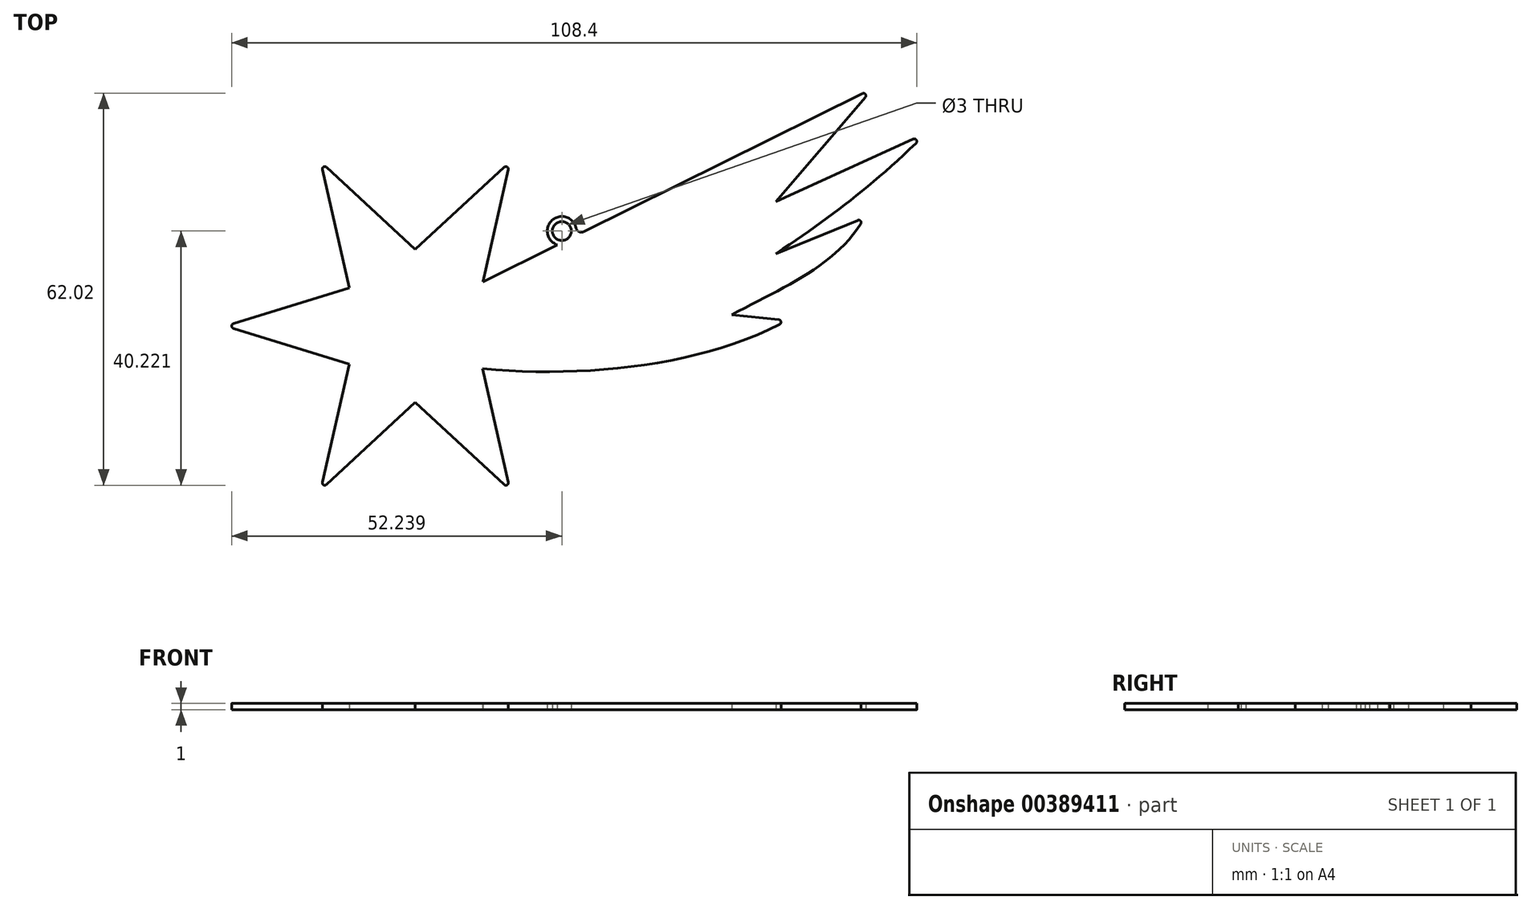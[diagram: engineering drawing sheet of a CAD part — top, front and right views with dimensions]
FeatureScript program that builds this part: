
annotation { "Feature Type Name" : "Feature", "Feature Type Description" : "" }
export const myFeature = defineFeature(function(context is Context, id is Id, definition is map)
    precondition{}
    {
        {
            var Q0;
            Q0=qCreatedBy(makeId("Top.planeOp"),FACE);
            var sketch = newSketch(context, id + "F0", { "sketchPlane" : qUnion([Q0])});
            skCircle(sketch, "E0.cCircle", {"center": v(0, 0) * mm, "radius": 30 * mm, "construction": true});
            skLineSegment(sketch, "E0.0", {"start": v(-30, 0) * mm, "end": v(-15, 25.98) * mm, "construction": true});
            skLineSegment(sketch, "E0.1", {"start": v(-15, 25.98) * mm, "end": v(15, 25.98) * mm, "construction": true});
            skLineSegment(sketch, "E0.2", {"start": v(15, 25.98) * mm, "end": v(30, 0) * mm, "construction": true});
            skLineSegment(sketch, "E0.3", {"start": v(30, 0) * mm, "end": v(15, -25.98) * mm, "construction": true});
            skLineSegment(sketch, "E0.4", {"start": v(15, -25.98) * mm, "end": v(-15, -25.98) * mm, "construction": true});
            skLineSegment(sketch, "E0.5", {"start": v(-15, -25.98) * mm, "end": v(-30, 0) * mm, "construction": true});
            skCircle(sketch, "E1.cCircle", {"center": v(0, 0) * mm, "radius": 12.09 * mm, "construction": true});
            skLineSegment(sketch, "E1.0", {"start": v(0, 12.09) * mm, "end": v(10.47, 6.04) * mm, "construction": true});
            skLineSegment(sketch, "E1.1", {"start": v(10.47, 6.04) * mm, "end": v(10.47, -6.04) * mm, "construction": true});
            skLineSegment(sketch, "E1.2", {"start": v(10.47, -6.04) * mm, "end": v(0, -12.09) * mm, "construction": true});
            skLineSegment(sketch, "E1.3", {"start": v(0, -12.09) * mm, "end": v(-10.47, -6.04) * mm, "construction": true});
            skLineSegment(sketch, "E1.4", {"start": v(-10.47, -6.04) * mm, "end": v(-10.47, 6.04) * mm, "construction": true});
            skLineSegment(sketch, "E1.5", {"start": v(-10.47, 6.04) * mm, "end": v(0, 12.09) * mm, "construction": true});
            skLineSegment(sketch, "E2", {"start": v(-15, 25.98) * mm, "end": v(-10.47, 6.04) * mm});
            skLineSegment(sketch, "E3", {"start": v(-30, 0) * mm, "end": v(-10.47, 6.04) * mm});
            skLineSegment(sketch, "E4", {"start": v(-30, 0) * mm, "end": v(-10.47, -6.04) * mm});
            skLineSegment(sketch, "E5", {"start": v(-10.47, -6.04) * mm, "end": v(-15, -25.98) * mm});
            skLineSegment(sketch, "E6", {"start": v(-15, -25.98) * mm, "end": v(0, -12.09) * mm});
            skLineSegment(sketch, "E7", {"start": v(0, -12.09) * mm, "end": v(15, -25.98) * mm});
            skLineSegment(sketch, "E8", {"start": v(15, -25.98) * mm, "end": v(10.47, -6.04) * mm});
            skLineSegment(sketch, "E9", {"start": v(10.47, -6.04) * mm, "end": v(30, 0) * mm});
            skLineSegment(sketch, "E10", {"start": v(30, 0) * mm, "end": v(10.47, 6.04) * mm});
            skLineSegment(sketch, "E11", {"start": v(10.47, 6.04) * mm, "end": v(15, 25.98) * mm});
            skLineSegment(sketch, "E12", {"start": v(15, 25.98) * mm, "end": v(0, 12.09) * mm});
            skLineSegment(sketch, "E13", {"start": v(0, 12.09) * mm, "end": v(-15, 25.98) * mm});
            skSolve(sketch);
        }
        {
            var Q0;
            Q0=qCreatedBy(makeId("Top.planeOp"),FACE);
            var sketch = newSketch(context, id + "F1", { "sketchPlane" : qUnion([Q0])});
            skLineSegment(sketch, "E14", {"start": v(7.39, 5.35) * mm, "end": v(72.49, 37.65) * mm});
            skFitSpline(sketch, "E15", {"points": [v(72.49, 37.65) * mm, v(57.07, 19.7) * mm], "startDerivative": vector(-15.42, -17.95) * mm, "endDerivative": vector(-15.42, -17.95) * mm});
            skFitSpline(sketch, "E16", {"points": [v(57.07, 19.7) * mm, v(80.89, 30.51) * mm], "startDerivative": vector(23.81, 10.81) * mm, "endDerivative": vector(23.81, 10.81) * mm});
            skFitSpline(sketch, "E17", {"points": [v(80.89, 30.51) * mm, v(57.07, 11.41) * mm], "startDerivative": vector(-25.7, -25.23) * mm, "endDerivative": vector(-26.86, -18.25) * mm});
            skFitSpline(sketch, "E18", {"points": [v(57.07, 11.41) * mm, v(71.1, 17.17) * mm], "startDerivative": vector(14.04, 5.75) * mm, "endDerivative": vector(14.04, 5.75) * mm});
            skFitSpline(sketch, "E19", {"points": [v(71.1, 17.17) * mm, v(50.05, 1.75) * mm], "startDerivative": vector(-12.49, -22.5) * mm, "endDerivative": vector(-25.34, -13.6) * mm});
            skFitSpline(sketch, "E20", {"points": [v(50.05, 1.75) * mm, v(58.82, 0.86) * mm], "startDerivative": vector(8.76, -0.9) * mm, "endDerivative": vector(8.76, -0.9) * mm});
            skFitSpline(sketch, "E21", {"points": [v(58.82, 0.86) * mm, v(7.78, -6.48) * mm], "startDerivative": vector(-41.96, -22.87) * mm, "endDerivative": vector(-51.14, 5.99) * mm});
            skLineSegment(sketch, "E22", {"start": v(7.78, -6.48) * mm, "end": v(7.39, 5.35) * mm});
            skSolve(sketch);
        }
        {
            var Q0;
            Q0=makeQuery(id+"F0.imprint","IMPRINT",FACE,{"disambiguationData":[TD([[makeQuery(id+"F0.imprint","IMPRINT",EDGE,{"derivedFrom":sQuery(id+"F0.wireOp",EDGE,"E2")}),1.0]])]});
            extrude(context, id + "F2", {"entities" : qUnion([Q0]), "depth" : 1 * mm});
        }
        {
            var Q0;
            Q0=qSketchRegion(id+"F1",true);
            extrude(context, id + "F3", {"entities" : qUnion([Q0]), "operationType" : NewBodyOperationType.ADD, "depth" : 1 * mm});
        }
        {
            var Q0;
            Q0=makeQuery(id+"F3.boolean.opBoolean","MERGE",FACE,{"derivedFrom":[makeQuery(id+"F2.opExtrude","CAP_FACE",FACE,{"disambiguationData":[OSD([sQuery(id+"F0.wireOp",EDGE,"E2"),sQuery(id+"F0.wireOp",EDGE,"E3"),sQuery(id+"F0.wireOp",EDGE,"E4"),sQuery(id+"F0.wireOp",EDGE,"E5"),sQuery(id+"F0.wireOp",EDGE,"E6"),sQuery(id+"F0.wireOp",EDGE,"E7"),sQuery(id+"F0.wireOp",EDGE,"E8"),sQuery(id+"F0.wireOp",EDGE,"E9"),sQuery(id+"F0.wireOp",EDGE,"E10"),sQuery(id+"F0.wireOp",EDGE,"E11"),sQuery(id+"F0.wireOp",EDGE,"E12"),sQuery(id+"F0.wireOp",EDGE,"E13")])],"isStart":true}),makeQuery(id+"F3.opExtrude","CAP_FACE",FACE,{"disambiguationData":[OSD([sQuery(id+"F1.wireOp",EDGE,"E14"),sQuery(id+"F1.wireOp",EDGE,"E15"),sQuery(id+"F1.wireOp",EDGE,"E16"),sQuery(id+"F1.wireOp",EDGE,"E17"),sQuery(id+"F1.wireOp",EDGE,"E18"),sQuery(id+"F1.wireOp",EDGE,"E19"),sQuery(id+"F1.wireOp",EDGE,"E20"),sQuery(id+"F1.wireOp",EDGE,"E21"),sQuery(id+"F1.wireOp",EDGE,"E22")])],"isStart":true})]});
            var sketch = newSketch(context, id + "F4", { "sketchPlane" : qUnion([Q0])});
            skCircle(sketch, "E23", {"center": v(23.19, -15.01) * mm, "radius": 2.3 * mm});
            skCircle(sketch, "E24", {"center": v(23.19, -15.01) * mm, "radius": 1.5 * mm});
            skSolve(sketch);
        }
        {
            var Q0;
            {var subQ4=sQuery(id+"F4.wireOp",EDGE,"E24");Q0=makeQuery(id+"F4.imprint","IMPRINT",FACE,{"disambiguationData":[TD([[makeQuery(id+"F4.imprint","IMPRINT",EDGE,{"derivedFrom":subQ4}),-1.0]])]});}
            extrude(context, id + "F5", {"entities" : qUnion([Q0]), "operationType" : NewBodyOperationType.ADD, "oppositeDirection" : true, "depth" : 1 * mm});
        }
        {
            var Q0;
            {var subQ0=sQuery(id+"F4.wireOp",EDGE,"E23");var subQ1=sQuery(id+"F1.wireOp",EDGE,"E14");Q0=makeQuery(id+"F5.opExtrude","SWEPT_EDGE",EDGE,{"disambiguationData":[OSD([subQ1,subQ0]),TDD([makeQuery(id+"F4.imprint","INTERSECT",VERTEX,{"disambiguationData":[OD(1.0)],"derivedFrom":[makeQuery(id+"F3.opExtrude","CAP_EDGE",EDGE,{"disambiguationData":[OSD([subQ1])],"isStart":true}),subQ0]})])]});}
            var Q1;
            {var subQ0=sQuery(id+"F4.wireOp",EDGE,"E23");var subQ1=sQuery(id+"F1.wireOp",EDGE,"E14");Q1=makeQuery(id+"F5.opExtrude","SWEPT_EDGE",EDGE,{"disambiguationData":[OSD([subQ1,subQ0]),TDD([makeQuery(id+"F4.imprint","INTERSECT",VERTEX,{"disambiguationData":[OD(0.0)],"derivedFrom":[makeQuery(id+"F3.opExtrude","CAP_EDGE",EDGE,{"disambiguationData":[OSD([subQ1])],"isStart":true}),subQ0]})])]});}
            fillet(context, id + "F6", {"entities" : qUnion([Q0, Q1]), "radius" : 0.86 * mm, "tangentPropagation" : true, "allowEdgeOverflow" : false});
        }
        {
            var Q0;
            Q0=makeQuery(id+"F2.opExtrude","SWEPT_EDGE",EDGE,{"disambiguationData":[OSD([sQuery(id+"F0.wireOp",EDGE,"E11"),sQuery(id+"F0.wireOp",EDGE,"E12")])]});
            var Q1;
            Q1=makeQuery(id+"F2.opExtrude","SWEPT_EDGE",EDGE,{"disambiguationData":[OSD([sQuery(id+"F0.wireOp",EDGE,"E2"),sQuery(id+"F0.wireOp",EDGE,"E13")])]});
            var Q2;
            Q2=makeQuery(id+"F2.opExtrude","SWEPT_EDGE",EDGE,{"disambiguationData":[OSD([sQuery(id+"F0.wireOp",EDGE,"E3"),sQuery(id+"F0.wireOp",EDGE,"E4")])]});
            var Q3;
            Q3=makeQuery(id+"F2.opExtrude","SWEPT_EDGE",EDGE,{"disambiguationData":[OSD([sQuery(id+"F0.wireOp",EDGE,"E5"),sQuery(id+"F0.wireOp",EDGE,"E6")])]});
            var Q4;
            Q4=makeQuery(id+"F2.opExtrude","SWEPT_EDGE",EDGE,{"disambiguationData":[OSD([sQuery(id+"F0.wireOp",EDGE,"E7"),sQuery(id+"F0.wireOp",EDGE,"E8")])]});
            var Q5;
            Q5=makeQuery(id+"F3.opExtrude","SWEPT_EDGE",EDGE,{"disambiguationData":[OSD([sQuery(id+"F1.wireOp",EDGE,"E14"),sQuery(id+"F1.wireOp",EDGE,"E15")])]});
            var Q6;
            Q6=makeQuery(id+"F3.opExtrude","SWEPT_EDGE",EDGE,{"disambiguationData":[OSD([sQuery(id+"F1.wireOp",EDGE,"E16"),sQuery(id+"F1.wireOp",EDGE,"E17")])]});
            var Q7;
            Q7=makeQuery(id+"F3.opExtrude","SWEPT_EDGE",EDGE,{"disambiguationData":[OSD([sQuery(id+"F1.wireOp",EDGE,"E18"),sQuery(id+"F1.wireOp",EDGE,"E19")])]});
            var Q8;
            Q8=makeQuery(id+"F3.opExtrude","SWEPT_EDGE",EDGE,{"disambiguationData":[OSD([sQuery(id+"F1.wireOp",EDGE,"E20"),sQuery(id+"F1.wireOp",EDGE,"E21")])]});
            fillet(context, id + "F7", {"entities" : qUnion([Q0, Q1, Q2, Q3, Q4, Q5, Q6, Q7, Q8]), "radius" : 0.4 * mm, "tangentPropagation" : true, "allowEdgeOverflow" : false});
        }
    });
